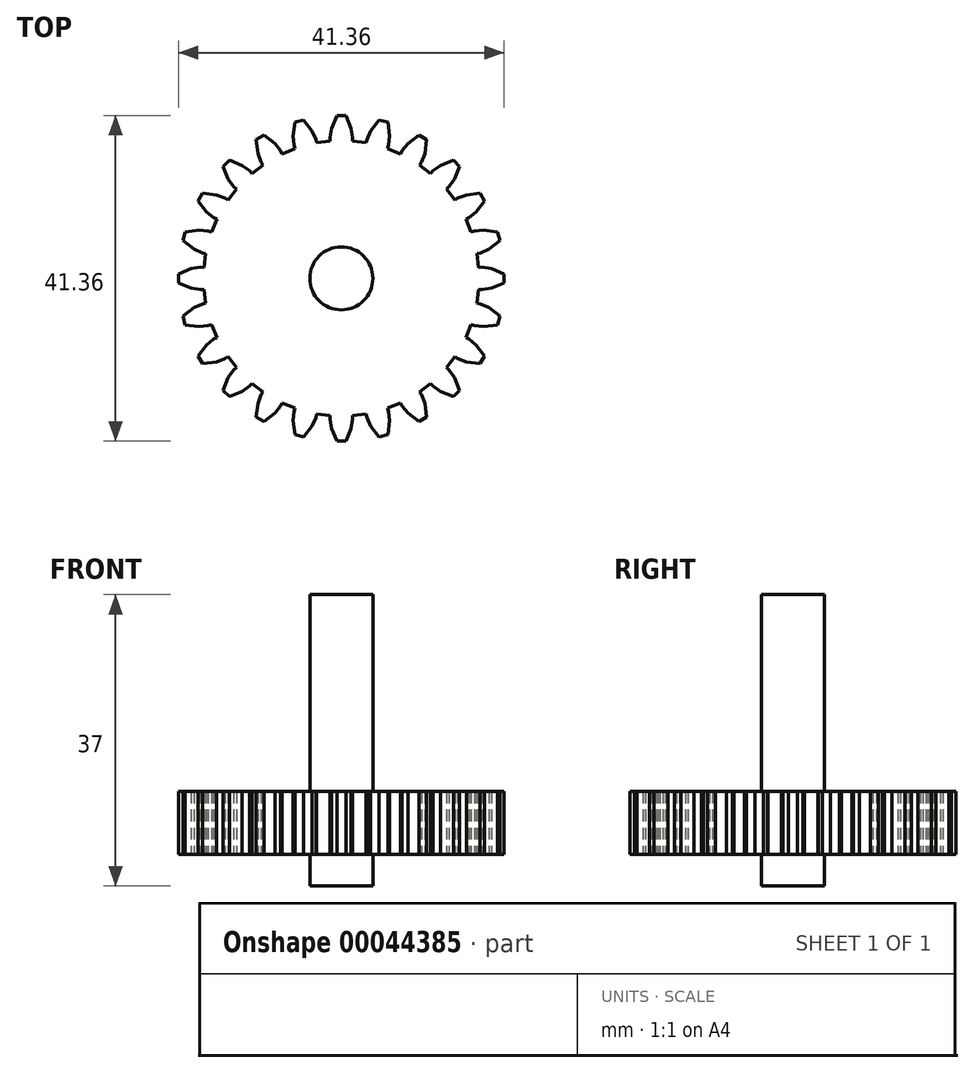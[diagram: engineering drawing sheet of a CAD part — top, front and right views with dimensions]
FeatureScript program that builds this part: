
annotation { "Feature Type Name" : "Feature", "Feature Type Description" : "" }
export const myFeature = defineFeature(function(context is Context, id is Id, definition is map)
    precondition{}
    {
        {
            var Q0;
            Q0=qCreatedBy(makeId("Top.planeOp"),FACE);
            var sketch = newSketch(context, id + "F0", { "sketchPlane" : qUnion([Q0])});
            skLineSegment(sketch, "E0", {"start": v(17.45, 1.4) * mm, "end": v(17.89, 1.44) * mm});
            skLineSegment(sketch, "E1", {"start": v(17.89, 1.44) * mm, "end": v(19.06, 1.25) * mm});
            skLineSegment(sketch, "E2", {"start": v(19.06, 1.25) * mm, "end": v(20.68, 0.57) * mm});
            skLineSegment(sketch, "E3", {"start": v(20.68, 0.57) * mm, "end": v(20.68, -0.57) * mm});
            skLineSegment(sketch, "E4", {"start": v(20.68, -0.57) * mm, "end": v(19.06, -1.25) * mm});
            skLineSegment(sketch, "E5", {"start": v(19.06, -1.25) * mm, "end": v(17.89, -1.44) * mm});
            skLineSegment(sketch, "E6", {"start": v(17.89, -1.44) * mm, "end": v(17.45, -1.4) * mm});
            skLineSegment(sketch, "E7", {"start": v(17.45, -1.4) * mm, "end": v(17.22, -3.16) * mm});
            skLineSegment(sketch, "E8", {"start": v(17.22, -3.16) * mm, "end": v(17.65, -3.24) * mm});
            skLineSegment(sketch, "E9", {"start": v(17.65, -3.24) * mm, "end": v(18.73, -3.73) * mm});
            skLineSegment(sketch, "E10", {"start": v(18.73, -3.73) * mm, "end": v(20.12, -4.8) * mm});
            skLineSegment(sketch, "E11", {"start": v(20.12, -4.8) * mm, "end": v(19.83, -5.9) * mm});
            skLineSegment(sketch, "E12", {"start": v(19.83, -5.9) * mm, "end": v(18.09, -6.14) * mm});
            skLineSegment(sketch, "E13", {"start": v(18.09, -6.14) * mm, "end": v(16.9, -6.02) * mm});
            skLineSegment(sketch, "E14", {"start": v(16.9, -6.02) * mm, "end": v(16.5, -5.87) * mm});
            skLineSegment(sketch, "E15", {"start": v(16.5, -5.87) * mm, "end": v(15.82, -7.5) * mm});
            skLineSegment(sketch, "E16", {"start": v(15.82, -7.5) * mm, "end": v(16.21, -7.7) * mm});
            skLineSegment(sketch, "E17", {"start": v(16.21, -7.7) * mm, "end": v(17.13, -8.45) * mm});
            skLineSegment(sketch, "E18", {"start": v(17.13, -8.45) * mm, "end": v(18.2, -9.85) * mm});
            skLineSegment(sketch, "E19", {"start": v(18.2, -9.85) * mm, "end": v(17.63, -10.83) * mm});
            skLineSegment(sketch, "E20", {"start": v(17.63, -10.83) * mm, "end": v(15.88, -10.61) * mm});
            skLineSegment(sketch, "E21", {"start": v(15.88, -10.61) * mm, "end": v(14.77, -10.2) * mm});
            skLineSegment(sketch, "E22", {"start": v(14.77, -10.2) * mm, "end": v(14.4, -9.94) * mm});
            skLineSegment(sketch, "E23", {"start": v(14.4, -9.94) * mm, "end": v(13.33, -11.35) * mm});
            skLineSegment(sketch, "E24", {"start": v(13.33, -11.35) * mm, "end": v(13.67, -11.63) * mm});
            skLineSegment(sketch, "E25", {"start": v(13.67, -11.63) * mm, "end": v(14.36, -12.6) * mm});
            skLineSegment(sketch, "E26", {"start": v(14.36, -12.6) * mm, "end": v(15.03, -14.22) * mm});
            skLineSegment(sketch, "E27", {"start": v(15.03, -14.22) * mm, "end": v(14.22, -15.03) * mm});
            skLineSegment(sketch, "E28", {"start": v(14.22, -15.03) * mm, "end": v(12.6, -14.36) * mm});
            skLineSegment(sketch, "E29", {"start": v(12.6, -14.36) * mm, "end": v(11.63, -13.67) * mm});
            skLineSegment(sketch, "E30", {"start": v(11.63, -13.67) * mm, "end": v(11.35, -13.33) * mm});
            skLineSegment(sketch, "E31", {"start": v(11.35, -13.33) * mm, "end": v(9.94, -14.4) * mm});
            skLineSegment(sketch, "E32", {"start": v(9.94, -14.4) * mm, "end": v(10.2, -14.77) * mm});
            skLineSegment(sketch, "E33", {"start": v(10.2, -14.77) * mm, "end": v(10.61, -15.88) * mm});
            skLineSegment(sketch, "E34", {"start": v(10.61, -15.88) * mm, "end": v(10.83, -17.63) * mm});
            skLineSegment(sketch, "E35", {"start": v(10.83, -17.63) * mm, "end": v(9.85, -18.2) * mm});
            skLineSegment(sketch, "E36", {"start": v(9.85, -18.2) * mm, "end": v(8.45, -17.13) * mm});
            skLineSegment(sketch, "E37", {"start": v(8.45, -17.13) * mm, "end": v(7.7, -16.21) * mm});
            skLineSegment(sketch, "E38", {"start": v(7.7, -16.21) * mm, "end": v(7.5, -15.82) * mm});
            skLineSegment(sketch, "E39", {"start": v(7.5, -15.82) * mm, "end": v(5.87, -16.5) * mm});
            skLineSegment(sketch, "E40", {"start": v(5.87, -16.5) * mm, "end": v(6.02, -16.9) * mm});
            skLineSegment(sketch, "E41", {"start": v(6.02, -16.9) * mm, "end": v(6.14, -18.09) * mm});
            skLineSegment(sketch, "E42", {"start": v(6.14, -18.09) * mm, "end": v(5.9, -19.83) * mm});
            skLineSegment(sketch, "E43", {"start": v(5.9, -19.83) * mm, "end": v(4.8, -20.12) * mm});
            skLineSegment(sketch, "E44", {"start": v(4.8, -20.12) * mm, "end": v(3.73, -18.73) * mm});
            skLineSegment(sketch, "E45", {"start": v(3.73, -18.73) * mm, "end": v(3.24, -17.65) * mm});
            skLineSegment(sketch, "E46", {"start": v(3.24, -17.65) * mm, "end": v(3.16, -17.22) * mm});
            skLineSegment(sketch, "E47", {"start": v(3.16, -17.22) * mm, "end": v(1.4, -17.45) * mm});
            skLineSegment(sketch, "E48", {"start": v(1.4, -17.45) * mm, "end": v(1.44, -17.89) * mm});
            skLineSegment(sketch, "E49", {"start": v(1.44, -17.89) * mm, "end": v(1.25, -19.06) * mm});
            skLineSegment(sketch, "E50", {"start": v(1.25, -19.06) * mm, "end": v(0.57, -20.68) * mm});
            skLineSegment(sketch, "E51", {"start": v(0.57, -20.68) * mm, "end": v(-0.57, -20.68) * mm});
            skLineSegment(sketch, "E52", {"start": v(-0.57, -20.68) * mm, "end": v(-1.25, -19.06) * mm});
            skLineSegment(sketch, "E53", {"start": v(-1.25, -19.06) * mm, "end": v(-1.44, -17.89) * mm});
            skLineSegment(sketch, "E54", {"start": v(-1.44, -17.89) * mm, "end": v(-1.4, -17.45) * mm});
            skLineSegment(sketch, "E55", {"start": v(-1.4, -17.45) * mm, "end": v(-3.16, -17.22) * mm});
            skLineSegment(sketch, "E56", {"start": v(-3.16, -17.22) * mm, "end": v(-3.24, -17.65) * mm});
            skLineSegment(sketch, "E57", {"start": v(-3.24, -17.65) * mm, "end": v(-3.73, -18.73) * mm});
            skLineSegment(sketch, "E58", {"start": v(-3.73, -18.73) * mm, "end": v(-4.8, -20.12) * mm});
            skLineSegment(sketch, "E59", {"start": v(-4.8, -20.12) * mm, "end": v(-5.9, -19.83) * mm});
            skLineSegment(sketch, "E60", {"start": v(-5.9, -19.83) * mm, "end": v(-6.14, -18.09) * mm});
            skLineSegment(sketch, "E61", {"start": v(-6.14, -18.09) * mm, "end": v(-6.02, -16.9) * mm});
            skLineSegment(sketch, "E62", {"start": v(-6.02, -16.9) * mm, "end": v(-5.87, -16.5) * mm});
            skLineSegment(sketch, "E63", {"start": v(-5.87, -16.5) * mm, "end": v(-7.5, -15.82) * mm});
            skLineSegment(sketch, "E64", {"start": v(-7.5, -15.82) * mm, "end": v(-7.7, -16.21) * mm});
            skLineSegment(sketch, "E65", {"start": v(-7.7, -16.21) * mm, "end": v(-8.45, -17.13) * mm});
            skLineSegment(sketch, "E66", {"start": v(-8.45, -17.13) * mm, "end": v(-9.85, -18.2) * mm});
            skLineSegment(sketch, "E67", {"start": v(-9.85, -18.2) * mm, "end": v(-10.83, -17.63) * mm});
            skLineSegment(sketch, "E68", {"start": v(-10.83, -17.63) * mm, "end": v(-10.61, -15.88) * mm});
            skLineSegment(sketch, "E69", {"start": v(-10.61, -15.88) * mm, "end": v(-10.2, -14.77) * mm});
            skLineSegment(sketch, "E70", {"start": v(-10.2, -14.77) * mm, "end": v(-9.94, -14.4) * mm});
            skLineSegment(sketch, "E71", {"start": v(-9.94, -14.4) * mm, "end": v(-11.35, -13.33) * mm});
            skLineSegment(sketch, "E72", {"start": v(-11.35, -13.33) * mm, "end": v(-11.63, -13.67) * mm});
            skLineSegment(sketch, "E73", {"start": v(-11.63, -13.67) * mm, "end": v(-12.6, -14.36) * mm});
            skLineSegment(sketch, "E74", {"start": v(-12.6, -14.36) * mm, "end": v(-14.22, -15.03) * mm});
            skLineSegment(sketch, "E75", {"start": v(-14.22, -15.03) * mm, "end": v(-15.03, -14.22) * mm});
            skLineSegment(sketch, "E76", {"start": v(-15.03, -14.22) * mm, "end": v(-14.36, -12.6) * mm});
            skLineSegment(sketch, "E77", {"start": v(-14.36, -12.6) * mm, "end": v(-13.67, -11.63) * mm});
            skLineSegment(sketch, "E78", {"start": v(-13.67, -11.63) * mm, "end": v(-13.33, -11.35) * mm});
            skLineSegment(sketch, "E79", {"start": v(-13.33, -11.35) * mm, "end": v(-14.4, -9.94) * mm});
            skLineSegment(sketch, "E80", {"start": v(-14.4, -9.94) * mm, "end": v(-14.77, -10.2) * mm});
            skLineSegment(sketch, "E81", {"start": v(-14.77, -10.2) * mm, "end": v(-15.88, -10.61) * mm});
            skLineSegment(sketch, "E82", {"start": v(-15.88, -10.61) * mm, "end": v(-17.63, -10.83) * mm});
            skLineSegment(sketch, "E83", {"start": v(-17.63, -10.83) * mm, "end": v(-18.2, -9.85) * mm});
            skLineSegment(sketch, "E84", {"start": v(-18.2, -9.85) * mm, "end": v(-17.13, -8.45) * mm});
            skLineSegment(sketch, "E85", {"start": v(-17.13, -8.45) * mm, "end": v(-16.21, -7.7) * mm});
            skLineSegment(sketch, "E86", {"start": v(-16.21, -7.7) * mm, "end": v(-15.82, -7.5) * mm});
            skLineSegment(sketch, "E87", {"start": v(-15.82, -7.5) * mm, "end": v(-16.5, -5.87) * mm});
            skLineSegment(sketch, "E88", {"start": v(-16.5, -5.87) * mm, "end": v(-16.9, -6.02) * mm});
            skLineSegment(sketch, "E89", {"start": v(-16.9, -6.02) * mm, "end": v(-18.09, -6.14) * mm});
            skLineSegment(sketch, "E90", {"start": v(-18.09, -6.14) * mm, "end": v(-19.83, -5.9) * mm});
            skLineSegment(sketch, "E91", {"start": v(-19.83, -5.9) * mm, "end": v(-20.12, -4.8) * mm});
            skLineSegment(sketch, "E92", {"start": v(-20.12, -4.8) * mm, "end": v(-18.73, -3.73) * mm});
            skLineSegment(sketch, "E93", {"start": v(-18.73, -3.73) * mm, "end": v(-17.65, -3.24) * mm});
            skLineSegment(sketch, "E94", {"start": v(-17.65, -3.24) * mm, "end": v(-17.22, -3.16) * mm});
            skLineSegment(sketch, "E95", {"start": v(-17.22, -3.16) * mm, "end": v(-17.45, -1.4) * mm});
            skLineSegment(sketch, "E96", {"start": v(-17.45, -1.4) * mm, "end": v(-17.89, -1.44) * mm});
            skLineSegment(sketch, "E97", {"start": v(-17.89, -1.44) * mm, "end": v(-19.06, -1.25) * mm});
            skLineSegment(sketch, "E98", {"start": v(-19.06, -1.25) * mm, "end": v(-20.68, -0.57) * mm});
            skLineSegment(sketch, "E99", {"start": v(-20.68, -0.57) * mm, "end": v(-20.68, 0.57) * mm});
            skLineSegment(sketch, "E100", {"start": v(-20.68, 0.57) * mm, "end": v(-19.06, 1.25) * mm});
            skLineSegment(sketch, "E101", {"start": v(-19.06, 1.25) * mm, "end": v(-17.89, 1.44) * mm});
            skLineSegment(sketch, "E102", {"start": v(-17.89, 1.44) * mm, "end": v(-17.45, 1.4) * mm});
            skLineSegment(sketch, "E103", {"start": v(-17.45, 1.4) * mm, "end": v(-17.22, 3.16) * mm});
            skLineSegment(sketch, "E104", {"start": v(-17.22, 3.16) * mm, "end": v(-17.65, 3.24) * mm});
            skLineSegment(sketch, "E105", {"start": v(-17.65, 3.24) * mm, "end": v(-18.73, 3.73) * mm});
            skLineSegment(sketch, "E106", {"start": v(-18.73, 3.73) * mm, "end": v(-20.12, 4.8) * mm});
            skLineSegment(sketch, "E107", {"start": v(-20.12, 4.8) * mm, "end": v(-19.83, 5.9) * mm});
            skLineSegment(sketch, "E108", {"start": v(-19.83, 5.9) * mm, "end": v(-18.09, 6.14) * mm});
            skLineSegment(sketch, "E109", {"start": v(-18.09, 6.14) * mm, "end": v(-16.9, 6.02) * mm});
            skLineSegment(sketch, "E110", {"start": v(-16.9, 6.02) * mm, "end": v(-16.5, 5.87) * mm});
            skLineSegment(sketch, "E111", {"start": v(-16.5, 5.87) * mm, "end": v(-15.82, 7.5) * mm});
            skLineSegment(sketch, "E112", {"start": v(-15.82, 7.5) * mm, "end": v(-16.21, 7.7) * mm});
            skLineSegment(sketch, "E113", {"start": v(-16.21, 7.7) * mm, "end": v(-17.13, 8.45) * mm});
            skLineSegment(sketch, "E114", {"start": v(-17.13, 8.45) * mm, "end": v(-18.2, 9.85) * mm});
            skLineSegment(sketch, "E115", {"start": v(-18.2, 9.85) * mm, "end": v(-17.63, 10.83) * mm});
            skLineSegment(sketch, "E116", {"start": v(-17.63, 10.83) * mm, "end": v(-15.88, 10.61) * mm});
            skLineSegment(sketch, "E117", {"start": v(-15.88, 10.61) * mm, "end": v(-14.77, 10.2) * mm});
            skLineSegment(sketch, "E118", {"start": v(-14.77, 10.2) * mm, "end": v(-14.4, 9.94) * mm});
            skLineSegment(sketch, "E119", {"start": v(-14.4, 9.94) * mm, "end": v(-13.33, 11.35) * mm});
            skLineSegment(sketch, "E120", {"start": v(-13.33, 11.35) * mm, "end": v(-13.67, 11.63) * mm});
            skLineSegment(sketch, "E121", {"start": v(-13.67, 11.63) * mm, "end": v(-14.36, 12.6) * mm});
            skLineSegment(sketch, "E122", {"start": v(-14.36, 12.6) * mm, "end": v(-15.03, 14.22) * mm});
            skLineSegment(sketch, "E123", {"start": v(-15.03, 14.22) * mm, "end": v(-14.22, 15.03) * mm});
            skLineSegment(sketch, "E124", {"start": v(-14.22, 15.03) * mm, "end": v(-12.6, 14.36) * mm});
            skLineSegment(sketch, "E125", {"start": v(-12.6, 14.36) * mm, "end": v(-11.63, 13.67) * mm});
            skLineSegment(sketch, "E126", {"start": v(-11.63, 13.67) * mm, "end": v(-11.35, 13.33) * mm});
            skLineSegment(sketch, "E127", {"start": v(-11.35, 13.33) * mm, "end": v(-9.94, 14.4) * mm});
            skLineSegment(sketch, "E128", {"start": v(-9.94, 14.4) * mm, "end": v(-10.2, 14.77) * mm});
            skLineSegment(sketch, "E129", {"start": v(-10.2, 14.77) * mm, "end": v(-10.61, 15.88) * mm});
            skLineSegment(sketch, "E130", {"start": v(-10.61, 15.88) * mm, "end": v(-10.83, 17.63) * mm});
            skLineSegment(sketch, "E131", {"start": v(-10.83, 17.63) * mm, "end": v(-9.85, 18.2) * mm});
            skLineSegment(sketch, "E132", {"start": v(-9.85, 18.2) * mm, "end": v(-8.45, 17.13) * mm});
            skLineSegment(sketch, "E133", {"start": v(-8.45, 17.13) * mm, "end": v(-7.7, 16.21) * mm});
            skLineSegment(sketch, "E134", {"start": v(-7.7, 16.21) * mm, "end": v(-7.5, 15.82) * mm});
            skLineSegment(sketch, "E135", {"start": v(-7.5, 15.82) * mm, "end": v(-5.87, 16.5) * mm});
            skLineSegment(sketch, "E136", {"start": v(-5.87, 16.5) * mm, "end": v(-6.02, 16.9) * mm});
            skLineSegment(sketch, "E137", {"start": v(-6.02, 16.9) * mm, "end": v(-6.14, 18.09) * mm});
            skLineSegment(sketch, "E138", {"start": v(-6.14, 18.09) * mm, "end": v(-5.9, 19.83) * mm});
            skLineSegment(sketch, "E139", {"start": v(-5.9, 19.83) * mm, "end": v(-4.8, 20.12) * mm});
            skLineSegment(sketch, "E140", {"start": v(-4.8, 20.12) * mm, "end": v(-3.73, 18.73) * mm});
            skLineSegment(sketch, "E141", {"start": v(-3.73, 18.73) * mm, "end": v(-3.24, 17.65) * mm});
            skLineSegment(sketch, "E142", {"start": v(-3.24, 17.65) * mm, "end": v(-3.16, 17.22) * mm});
            skLineSegment(sketch, "E143", {"start": v(-3.16, 17.22) * mm, "end": v(-1.4, 17.45) * mm});
            skLineSegment(sketch, "E144", {"start": v(-1.4, 17.45) * mm, "end": v(-1.44, 17.89) * mm});
            skLineSegment(sketch, "E145", {"start": v(-1.44, 17.89) * mm, "end": v(-1.25, 19.06) * mm});
            skLineSegment(sketch, "E146", {"start": v(-1.25, 19.06) * mm, "end": v(-0.57, 20.68) * mm});
            skLineSegment(sketch, "E147", {"start": v(-0.57, 20.68) * mm, "end": v(0.57, 20.68) * mm});
            skLineSegment(sketch, "E148", {"start": v(0.57, 20.68) * mm, "end": v(1.25, 19.06) * mm});
            skLineSegment(sketch, "E149", {"start": v(1.25, 19.06) * mm, "end": v(1.44, 17.89) * mm});
            skLineSegment(sketch, "E150", {"start": v(1.44, 17.89) * mm, "end": v(1.4, 17.45) * mm});
            skLineSegment(sketch, "E151", {"start": v(1.4, 17.45) * mm, "end": v(3.16, 17.22) * mm});
            skLineSegment(sketch, "E152", {"start": v(3.16, 17.22) * mm, "end": v(3.24, 17.65) * mm});
            skLineSegment(sketch, "E153", {"start": v(3.24, 17.65) * mm, "end": v(3.73, 18.73) * mm});
            skLineSegment(sketch, "E154", {"start": v(3.73, 18.73) * mm, "end": v(4.8, 20.12) * mm});
            skLineSegment(sketch, "E155", {"start": v(4.8, 20.12) * mm, "end": v(5.9, 19.83) * mm});
            skLineSegment(sketch, "E156", {"start": v(5.9, 19.83) * mm, "end": v(6.14, 18.09) * mm});
            skLineSegment(sketch, "E157", {"start": v(6.14, 18.09) * mm, "end": v(6.02, 16.9) * mm});
            skLineSegment(sketch, "E158", {"start": v(6.02, 16.9) * mm, "end": v(5.87, 16.5) * mm});
            skLineSegment(sketch, "E159", {"start": v(5.87, 16.5) * mm, "end": v(7.5, 15.82) * mm});
            skLineSegment(sketch, "E160", {"start": v(7.5, 15.82) * mm, "end": v(7.7, 16.21) * mm});
            skLineSegment(sketch, "E161", {"start": v(7.7, 16.21) * mm, "end": v(8.45, 17.13) * mm});
            skLineSegment(sketch, "E162", {"start": v(8.45, 17.13) * mm, "end": v(9.85, 18.2) * mm});
            skLineSegment(sketch, "E163", {"start": v(9.85, 18.2) * mm, "end": v(10.83, 17.63) * mm});
            skLineSegment(sketch, "E164", {"start": v(10.83, 17.63) * mm, "end": v(10.61, 15.88) * mm});
            skLineSegment(sketch, "E165", {"start": v(10.61, 15.88) * mm, "end": v(10.2, 14.77) * mm});
            skLineSegment(sketch, "E166", {"start": v(10.2, 14.77) * mm, "end": v(9.94, 14.4) * mm});
            skLineSegment(sketch, "E167", {"start": v(9.94, 14.4) * mm, "end": v(11.35, 13.33) * mm});
            skLineSegment(sketch, "E168", {"start": v(11.35, 13.33) * mm, "end": v(11.63, 13.67) * mm});
            skLineSegment(sketch, "E169", {"start": v(11.63, 13.67) * mm, "end": v(12.6, 14.36) * mm});
            skLineSegment(sketch, "E170", {"start": v(12.6, 14.36) * mm, "end": v(14.22, 15.03) * mm});
            skLineSegment(sketch, "E171", {"start": v(14.22, 15.03) * mm, "end": v(15.03, 14.22) * mm});
            skLineSegment(sketch, "E172", {"start": v(15.03, 14.22) * mm, "end": v(14.36, 12.6) * mm});
            skLineSegment(sketch, "E173", {"start": v(14.36, 12.6) * mm, "end": v(13.67, 11.63) * mm});
            skLineSegment(sketch, "E174", {"start": v(13.67, 11.63) * mm, "end": v(13.33, 11.35) * mm});
            skLineSegment(sketch, "E175", {"start": v(13.33, 11.35) * mm, "end": v(14.4, 9.94) * mm});
            skLineSegment(sketch, "E176", {"start": v(14.4, 9.94) * mm, "end": v(14.77, 10.2) * mm});
            skLineSegment(sketch, "E177", {"start": v(14.77, 10.2) * mm, "end": v(15.88, 10.61) * mm});
            skLineSegment(sketch, "E178", {"start": v(15.88, 10.61) * mm, "end": v(17.63, 10.83) * mm});
            skLineSegment(sketch, "E179", {"start": v(17.63, 10.83) * mm, "end": v(18.2, 9.85) * mm});
            skLineSegment(sketch, "E180", {"start": v(18.2, 9.85) * mm, "end": v(17.13, 8.45) * mm});
            skLineSegment(sketch, "E181", {"start": v(17.13, 8.45) * mm, "end": v(16.21, 7.7) * mm});
            skLineSegment(sketch, "E182", {"start": v(16.21, 7.7) * mm, "end": v(15.82, 7.5) * mm});
            skLineSegment(sketch, "E183", {"start": v(15.82, 7.5) * mm, "end": v(16.5, 5.87) * mm});
            skLineSegment(sketch, "E184", {"start": v(16.5, 5.87) * mm, "end": v(16.9, 6.02) * mm});
            skLineSegment(sketch, "E185", {"start": v(16.9, 6.02) * mm, "end": v(18.09, 6.14) * mm});
            skLineSegment(sketch, "E186", {"start": v(18.09, 6.14) * mm, "end": v(19.83, 5.9) * mm});
            skLineSegment(sketch, "E187", {"start": v(19.83, 5.9) * mm, "end": v(20.12, 4.8) * mm});
            skLineSegment(sketch, "E188", {"start": v(20.12, 4.8) * mm, "end": v(18.73, 3.73) * mm});
            skLineSegment(sketch, "E189", {"start": v(18.73, 3.73) * mm, "end": v(17.65, 3.24) * mm});
            skLineSegment(sketch, "E190", {"start": v(17.65, 3.24) * mm, "end": v(17.22, 3.16) * mm});
            skLineSegment(sketch, "E191", {"start": v(17.22, 3.16) * mm, "end": v(17.45, 1.4) * mm});
            skSolve(sketch);
        }
        {
            var Q0;
            Q0=makeQuery(id+"F0.imprint","IMPRINT",FACE,{"disambiguationData":[TD([[makeQuery(id+"F0.imprint","IMPRINT",EDGE,{"derivedFrom":sQuery(id+"F0.wireOp",EDGE,"E0")}),-1.0]])]});
            extrude(context, id + "F1", {"entities" : qUnion([Q0]), "depth" : 8 * mm});
        }
        {
            var Q0;
            Q0=makeQuery(id+"F1.opExtrude","CAP_FACE",FACE,{"disambiguationData":[OSD([sQuery(id+"F0.wireOp",EDGE,"E0"),sQuery(id+"F0.wireOp",EDGE,"E1"),sQuery(id+"F0.wireOp",EDGE,"E2"),sQuery(id+"F0.wireOp",EDGE,"E3"),sQuery(id+"F0.wireOp",EDGE,"E4"),sQuery(id+"F0.wireOp",EDGE,"E5"),sQuery(id+"F0.wireOp",EDGE,"E6"),sQuery(id+"F0.wireOp",EDGE,"E7"),sQuery(id+"F0.wireOp",EDGE,"E8"),sQuery(id+"F0.wireOp",EDGE,"E9"),sQuery(id+"F0.wireOp",EDGE,"E10"),sQuery(id+"F0.wireOp",EDGE,"E11"),sQuery(id+"F0.wireOp",EDGE,"E12"),sQuery(id+"F0.wireOp",EDGE,"E13"),sQuery(id+"F0.wireOp",EDGE,"E14"),sQuery(id+"F0.wireOp",EDGE,"E15"),sQuery(id+"F0.wireOp",EDGE,"E16"),sQuery(id+"F0.wireOp",EDGE,"E17"),sQuery(id+"F0.wireOp",EDGE,"E18"),sQuery(id+"F0.wireOp",EDGE,"E19"),sQuery(id+"F0.wireOp",EDGE,"E20"),sQuery(id+"F0.wireOp",EDGE,"E21"),sQuery(id+"F0.wireOp",EDGE,"E22"),sQuery(id+"F0.wireOp",EDGE,"E23"),sQuery(id+"F0.wireOp",EDGE,"E24"),sQuery(id+"F0.wireOp",EDGE,"E25"),sQuery(id+"F0.wireOp",EDGE,"E26"),sQuery(id+"F0.wireOp",EDGE,"E27"),sQuery(id+"F0.wireOp",EDGE,"E28"),sQuery(id+"F0.wireOp",EDGE,"E29"),sQuery(id+"F0.wireOp",EDGE,"E30"),sQuery(id+"F0.wireOp",EDGE,"E31"),sQuery(id+"F0.wireOp",EDGE,"E32"),sQuery(id+"F0.wireOp",EDGE,"E33"),sQuery(id+"F0.wireOp",EDGE,"E34"),sQuery(id+"F0.wireOp",EDGE,"E35"),sQuery(id+"F0.wireOp",EDGE,"E36"),sQuery(id+"F0.wireOp",EDGE,"E37"),sQuery(id+"F0.wireOp",EDGE,"E38"),sQuery(id+"F0.wireOp",EDGE,"E39"),sQuery(id+"F0.wireOp",EDGE,"E40"),sQuery(id+"F0.wireOp",EDGE,"E41"),sQuery(id+"F0.wireOp",EDGE,"E42"),sQuery(id+"F0.wireOp",EDGE,"E43"),sQuery(id+"F0.wireOp",EDGE,"E44"),sQuery(id+"F0.wireOp",EDGE,"E45"),sQuery(id+"F0.wireOp",EDGE,"E46"),sQuery(id+"F0.wireOp",EDGE,"E47"),sQuery(id+"F0.wireOp",EDGE,"E48"),sQuery(id+"F0.wireOp",EDGE,"E49"),sQuery(id+"F0.wireOp",EDGE,"E50"),sQuery(id+"F0.wireOp",EDGE,"E51"),sQuery(id+"F0.wireOp",EDGE,"E52"),sQuery(id+"F0.wireOp",EDGE,"E53"),sQuery(id+"F0.wireOp",EDGE,"E54"),sQuery(id+"F0.wireOp",EDGE,"E55"),sQuery(id+"F0.wireOp",EDGE,"E56"),sQuery(id+"F0.wireOp",EDGE,"E57"),sQuery(id+"F0.wireOp",EDGE,"E58"),sQuery(id+"F0.wireOp",EDGE,"E59"),sQuery(id+"F0.wireOp",EDGE,"E60"),sQuery(id+"F0.wireOp",EDGE,"E61"),sQuery(id+"F0.wireOp",EDGE,"E62"),sQuery(id+"F0.wireOp",EDGE,"E63"),sQuery(id+"F0.wireOp",EDGE,"E64"),sQuery(id+"F0.wireOp",EDGE,"E65"),sQuery(id+"F0.wireOp",EDGE,"E66"),sQuery(id+"F0.wireOp",EDGE,"E67"),sQuery(id+"F0.wireOp",EDGE,"E68"),sQuery(id+"F0.wireOp",EDGE,"E69"),sQuery(id+"F0.wireOp",EDGE,"E70"),sQuery(id+"F0.wireOp",EDGE,"E71"),sQuery(id+"F0.wireOp",EDGE,"E72"),sQuery(id+"F0.wireOp",EDGE,"E73"),sQuery(id+"F0.wireOp",EDGE,"E74"),sQuery(id+"F0.wireOp",EDGE,"E75"),sQuery(id+"F0.wireOp",EDGE,"E76"),sQuery(id+"F0.wireOp",EDGE,"E77"),sQuery(id+"F0.wireOp",EDGE,"E78"),sQuery(id+"F0.wireOp",EDGE,"E79"),sQuery(id+"F0.wireOp",EDGE,"E80"),sQuery(id+"F0.wireOp",EDGE,"E81"),sQuery(id+"F0.wireOp",EDGE,"E82"),sQuery(id+"F0.wireOp",EDGE,"E83"),sQuery(id+"F0.wireOp",EDGE,"E84"),sQuery(id+"F0.wireOp",EDGE,"E85"),sQuery(id+"F0.wireOp",EDGE,"E86"),sQuery(id+"F0.wireOp",EDGE,"E87"),sQuery(id+"F0.wireOp",EDGE,"E88"),sQuery(id+"F0.wireOp",EDGE,"E89"),sQuery(id+"F0.wireOp",EDGE,"E90"),sQuery(id+"F0.wireOp",EDGE,"E91"),sQuery(id+"F0.wireOp",EDGE,"E92"),sQuery(id+"F0.wireOp",EDGE,"E93"),sQuery(id+"F0.wireOp",EDGE,"E94"),sQuery(id+"F0.wireOp",EDGE,"E95"),sQuery(id+"F0.wireOp",EDGE,"E96"),sQuery(id+"F0.wireOp",EDGE,"E97"),sQuery(id+"F0.wireOp",EDGE,"E98"),sQuery(id+"F0.wireOp",EDGE,"E99"),sQuery(id+"F0.wireOp",EDGE,"E100"),sQuery(id+"F0.wireOp",EDGE,"E101"),sQuery(id+"F0.wireOp",EDGE,"E102"),sQuery(id+"F0.wireOp",EDGE,"E103"),sQuery(id+"F0.wireOp",EDGE,"E104"),sQuery(id+"F0.wireOp",EDGE,"E105"),sQuery(id+"F0.wireOp",EDGE,"E106"),sQuery(id+"F0.wireOp",EDGE,"E107"),sQuery(id+"F0.wireOp",EDGE,"E108"),sQuery(id+"F0.wireOp",EDGE,"E109"),sQuery(id+"F0.wireOp",EDGE,"E110"),sQuery(id+"F0.wireOp",EDGE,"E111"),sQuery(id+"F0.wireOp",EDGE,"E112"),sQuery(id+"F0.wireOp",EDGE,"E113"),sQuery(id+"F0.wireOp",EDGE,"E114"),sQuery(id+"F0.wireOp",EDGE,"E115"),sQuery(id+"F0.wireOp",EDGE,"E116"),sQuery(id+"F0.wireOp",EDGE,"E117"),sQuery(id+"F0.wireOp",EDGE,"E118"),sQuery(id+"F0.wireOp",EDGE,"E119"),sQuery(id+"F0.wireOp",EDGE,"E120"),sQuery(id+"F0.wireOp",EDGE,"E121"),sQuery(id+"F0.wireOp",EDGE,"E122"),sQuery(id+"F0.wireOp",EDGE,"E123"),sQuery(id+"F0.wireOp",EDGE,"E124"),sQuery(id+"F0.wireOp",EDGE,"E125"),sQuery(id+"F0.wireOp",EDGE,"E126"),sQuery(id+"F0.wireOp",EDGE,"E127"),sQuery(id+"F0.wireOp",EDGE,"E128"),sQuery(id+"F0.wireOp",EDGE,"E129"),sQuery(id+"F0.wireOp",EDGE,"E130"),sQuery(id+"F0.wireOp",EDGE,"E131"),sQuery(id+"F0.wireOp",EDGE,"E132"),sQuery(id+"F0.wireOp",EDGE,"E133"),sQuery(id+"F0.wireOp",EDGE,"E134"),sQuery(id+"F0.wireOp",EDGE,"E135"),sQuery(id+"F0.wireOp",EDGE,"E136"),sQuery(id+"F0.wireOp",EDGE,"E137"),sQuery(id+"F0.wireOp",EDGE,"E138"),sQuery(id+"F0.wireOp",EDGE,"E139"),sQuery(id+"F0.wireOp",EDGE,"E140"),sQuery(id+"F0.wireOp",EDGE,"E141"),sQuery(id+"F0.wireOp",EDGE,"E142"),sQuery(id+"F0.wireOp",EDGE,"E143"),sQuery(id+"F0.wireOp",EDGE,"E144"),sQuery(id+"F0.wireOp",EDGE,"E145"),sQuery(id+"F0.wireOp",EDGE,"E146"),sQuery(id+"F0.wireOp",EDGE,"E147"),sQuery(id+"F0.wireOp",EDGE,"E148"),sQuery(id+"F0.wireOp",EDGE,"E149"),sQuery(id+"F0.wireOp",EDGE,"E150"),sQuery(id+"F0.wireOp",EDGE,"E151"),sQuery(id+"F0.wireOp",EDGE,"E152"),sQuery(id+"F0.wireOp",EDGE,"E153"),sQuery(id+"F0.wireOp",EDGE,"E154"),sQuery(id+"F0.wireOp",EDGE,"E155"),sQuery(id+"F0.wireOp",EDGE,"E156"),sQuery(id+"F0.wireOp",EDGE,"E157"),sQuery(id+"F0.wireOp",EDGE,"E158"),sQuery(id+"F0.wireOp",EDGE,"E159"),sQuery(id+"F0.wireOp",EDGE,"E160"),sQuery(id+"F0.wireOp",EDGE,"E161"),sQuery(id+"F0.wireOp",EDGE,"E162"),sQuery(id+"F0.wireOp",EDGE,"E163"),sQuery(id+"F0.wireOp",EDGE,"E164"),sQuery(id+"F0.wireOp",EDGE,"E165"),sQuery(id+"F0.wireOp",EDGE,"E166"),sQuery(id+"F0.wireOp",EDGE,"E167"),sQuery(id+"F0.wireOp",EDGE,"E168"),sQuery(id+"F0.wireOp",EDGE,"E169"),sQuery(id+"F0.wireOp",EDGE,"E170"),sQuery(id+"F0.wireOp",EDGE,"E171"),sQuery(id+"F0.wireOp",EDGE,"E172"),sQuery(id+"F0.wireOp",EDGE,"E173"),sQuery(id+"F0.wireOp",EDGE,"E174"),sQuery(id+"F0.wireOp",EDGE,"E175"),sQuery(id+"F0.wireOp",EDGE,"E176"),sQuery(id+"F0.wireOp",EDGE,"E177"),sQuery(id+"F0.wireOp",EDGE,"E178"),sQuery(id+"F0.wireOp",EDGE,"E179"),sQuery(id+"F0.wireOp",EDGE,"E180"),sQuery(id+"F0.wireOp",EDGE,"E181"),sQuery(id+"F0.wireOp",EDGE,"E182"),sQuery(id+"F0.wireOp",EDGE,"E183"),sQuery(id+"F0.wireOp",EDGE,"E184"),sQuery(id+"F0.wireOp",EDGE,"E185"),sQuery(id+"F0.wireOp",EDGE,"E186"),sQuery(id+"F0.wireOp",EDGE,"E187"),sQuery(id+"F0.wireOp",EDGE,"E188"),sQuery(id+"F0.wireOp",EDGE,"E189"),sQuery(id+"F0.wireOp",EDGE,"E190"),sQuery(id+"F0.wireOp",EDGE,"E191")])],"isStart":false});
            var sketch = newSketch(context, id + "F2", { "sketchPlane" : qUnion([Q0])});
            skCircle(sketch, "E192", {"center": v(0, 0) * mm, "radius": 4 * mm});
            skSolve(sketch);
        }
        {
            var Q0;
            Q0=makeQuery(id+"F2.imprint","IMPRINT",FACE,{"disambiguationData":[TD([[makeQuery(id+"F2.imprint","IMPRINT",EDGE,{"derivedFrom":sQuery(id+"F2.wireOp",EDGE,"E192")}),1.0]])]});
            extrude(context, id + "F3", {"entities" : qUnion([Q0]), "operationType" : NewBodyOperationType.ADD, "depth" : 25 * mm});
        }
        {
            var Q0;
            Q0=makeQuery(id+"F1.opExtrude","CAP_FACE",FACE,{"disambiguationData":[OSD([sQuery(id+"F0.wireOp",EDGE,"E0"),sQuery(id+"F0.wireOp",EDGE,"E1"),sQuery(id+"F0.wireOp",EDGE,"E2"),sQuery(id+"F0.wireOp",EDGE,"E3"),sQuery(id+"F0.wireOp",EDGE,"E4"),sQuery(id+"F0.wireOp",EDGE,"E5"),sQuery(id+"F0.wireOp",EDGE,"E6"),sQuery(id+"F0.wireOp",EDGE,"E7"),sQuery(id+"F0.wireOp",EDGE,"E8"),sQuery(id+"F0.wireOp",EDGE,"E9"),sQuery(id+"F0.wireOp",EDGE,"E10"),sQuery(id+"F0.wireOp",EDGE,"E11"),sQuery(id+"F0.wireOp",EDGE,"E12"),sQuery(id+"F0.wireOp",EDGE,"E13"),sQuery(id+"F0.wireOp",EDGE,"E14"),sQuery(id+"F0.wireOp",EDGE,"E15"),sQuery(id+"F0.wireOp",EDGE,"E16"),sQuery(id+"F0.wireOp",EDGE,"E17"),sQuery(id+"F0.wireOp",EDGE,"E18"),sQuery(id+"F0.wireOp",EDGE,"E19"),sQuery(id+"F0.wireOp",EDGE,"E20"),sQuery(id+"F0.wireOp",EDGE,"E21"),sQuery(id+"F0.wireOp",EDGE,"E22"),sQuery(id+"F0.wireOp",EDGE,"E23"),sQuery(id+"F0.wireOp",EDGE,"E24"),sQuery(id+"F0.wireOp",EDGE,"E25"),sQuery(id+"F0.wireOp",EDGE,"E26"),sQuery(id+"F0.wireOp",EDGE,"E27"),sQuery(id+"F0.wireOp",EDGE,"E28"),sQuery(id+"F0.wireOp",EDGE,"E29"),sQuery(id+"F0.wireOp",EDGE,"E30"),sQuery(id+"F0.wireOp",EDGE,"E31"),sQuery(id+"F0.wireOp",EDGE,"E32"),sQuery(id+"F0.wireOp",EDGE,"E33"),sQuery(id+"F0.wireOp",EDGE,"E34"),sQuery(id+"F0.wireOp",EDGE,"E35"),sQuery(id+"F0.wireOp",EDGE,"E36"),sQuery(id+"F0.wireOp",EDGE,"E37"),sQuery(id+"F0.wireOp",EDGE,"E38"),sQuery(id+"F0.wireOp",EDGE,"E39"),sQuery(id+"F0.wireOp",EDGE,"E40"),sQuery(id+"F0.wireOp",EDGE,"E41"),sQuery(id+"F0.wireOp",EDGE,"E42"),sQuery(id+"F0.wireOp",EDGE,"E43"),sQuery(id+"F0.wireOp",EDGE,"E44"),sQuery(id+"F0.wireOp",EDGE,"E45"),sQuery(id+"F0.wireOp",EDGE,"E46"),sQuery(id+"F0.wireOp",EDGE,"E47"),sQuery(id+"F0.wireOp",EDGE,"E48"),sQuery(id+"F0.wireOp",EDGE,"E49"),sQuery(id+"F0.wireOp",EDGE,"E50"),sQuery(id+"F0.wireOp",EDGE,"E51"),sQuery(id+"F0.wireOp",EDGE,"E52"),sQuery(id+"F0.wireOp",EDGE,"E53"),sQuery(id+"F0.wireOp",EDGE,"E54"),sQuery(id+"F0.wireOp",EDGE,"E55"),sQuery(id+"F0.wireOp",EDGE,"E56"),sQuery(id+"F0.wireOp",EDGE,"E57"),sQuery(id+"F0.wireOp",EDGE,"E58"),sQuery(id+"F0.wireOp",EDGE,"E59"),sQuery(id+"F0.wireOp",EDGE,"E60"),sQuery(id+"F0.wireOp",EDGE,"E61"),sQuery(id+"F0.wireOp",EDGE,"E62"),sQuery(id+"F0.wireOp",EDGE,"E63"),sQuery(id+"F0.wireOp",EDGE,"E64"),sQuery(id+"F0.wireOp",EDGE,"E65"),sQuery(id+"F0.wireOp",EDGE,"E66"),sQuery(id+"F0.wireOp",EDGE,"E67"),sQuery(id+"F0.wireOp",EDGE,"E68"),sQuery(id+"F0.wireOp",EDGE,"E69"),sQuery(id+"F0.wireOp",EDGE,"E70"),sQuery(id+"F0.wireOp",EDGE,"E71"),sQuery(id+"F0.wireOp",EDGE,"E72"),sQuery(id+"F0.wireOp",EDGE,"E73"),sQuery(id+"F0.wireOp",EDGE,"E74"),sQuery(id+"F0.wireOp",EDGE,"E75"),sQuery(id+"F0.wireOp",EDGE,"E76"),sQuery(id+"F0.wireOp",EDGE,"E77"),sQuery(id+"F0.wireOp",EDGE,"E78"),sQuery(id+"F0.wireOp",EDGE,"E79"),sQuery(id+"F0.wireOp",EDGE,"E80"),sQuery(id+"F0.wireOp",EDGE,"E81"),sQuery(id+"F0.wireOp",EDGE,"E82"),sQuery(id+"F0.wireOp",EDGE,"E83"),sQuery(id+"F0.wireOp",EDGE,"E84"),sQuery(id+"F0.wireOp",EDGE,"E85"),sQuery(id+"F0.wireOp",EDGE,"E86"),sQuery(id+"F0.wireOp",EDGE,"E87"),sQuery(id+"F0.wireOp",EDGE,"E88"),sQuery(id+"F0.wireOp",EDGE,"E89"),sQuery(id+"F0.wireOp",EDGE,"E90"),sQuery(id+"F0.wireOp",EDGE,"E91"),sQuery(id+"F0.wireOp",EDGE,"E92"),sQuery(id+"F0.wireOp",EDGE,"E93"),sQuery(id+"F0.wireOp",EDGE,"E94"),sQuery(id+"F0.wireOp",EDGE,"E95"),sQuery(id+"F0.wireOp",EDGE,"E96"),sQuery(id+"F0.wireOp",EDGE,"E97"),sQuery(id+"F0.wireOp",EDGE,"E98"),sQuery(id+"F0.wireOp",EDGE,"E99"),sQuery(id+"F0.wireOp",EDGE,"E100"),sQuery(id+"F0.wireOp",EDGE,"E101"),sQuery(id+"F0.wireOp",EDGE,"E102"),sQuery(id+"F0.wireOp",EDGE,"E103"),sQuery(id+"F0.wireOp",EDGE,"E104"),sQuery(id+"F0.wireOp",EDGE,"E105"),sQuery(id+"F0.wireOp",EDGE,"E106"),sQuery(id+"F0.wireOp",EDGE,"E107"),sQuery(id+"F0.wireOp",EDGE,"E108"),sQuery(id+"F0.wireOp",EDGE,"E109"),sQuery(id+"F0.wireOp",EDGE,"E110"),sQuery(id+"F0.wireOp",EDGE,"E111"),sQuery(id+"F0.wireOp",EDGE,"E112"),sQuery(id+"F0.wireOp",EDGE,"E113"),sQuery(id+"F0.wireOp",EDGE,"E114"),sQuery(id+"F0.wireOp",EDGE,"E115"),sQuery(id+"F0.wireOp",EDGE,"E116"),sQuery(id+"F0.wireOp",EDGE,"E117"),sQuery(id+"F0.wireOp",EDGE,"E118"),sQuery(id+"F0.wireOp",EDGE,"E119"),sQuery(id+"F0.wireOp",EDGE,"E120"),sQuery(id+"F0.wireOp",EDGE,"E121"),sQuery(id+"F0.wireOp",EDGE,"E122"),sQuery(id+"F0.wireOp",EDGE,"E123"),sQuery(id+"F0.wireOp",EDGE,"E124"),sQuery(id+"F0.wireOp",EDGE,"E125"),sQuery(id+"F0.wireOp",EDGE,"E126"),sQuery(id+"F0.wireOp",EDGE,"E127"),sQuery(id+"F0.wireOp",EDGE,"E128"),sQuery(id+"F0.wireOp",EDGE,"E129"),sQuery(id+"F0.wireOp",EDGE,"E130"),sQuery(id+"F0.wireOp",EDGE,"E131"),sQuery(id+"F0.wireOp",EDGE,"E132"),sQuery(id+"F0.wireOp",EDGE,"E133"),sQuery(id+"F0.wireOp",EDGE,"E134"),sQuery(id+"F0.wireOp",EDGE,"E135"),sQuery(id+"F0.wireOp",EDGE,"E136"),sQuery(id+"F0.wireOp",EDGE,"E137"),sQuery(id+"F0.wireOp",EDGE,"E138"),sQuery(id+"F0.wireOp",EDGE,"E139"),sQuery(id+"F0.wireOp",EDGE,"E140"),sQuery(id+"F0.wireOp",EDGE,"E141"),sQuery(id+"F0.wireOp",EDGE,"E142"),sQuery(id+"F0.wireOp",EDGE,"E143"),sQuery(id+"F0.wireOp",EDGE,"E144"),sQuery(id+"F0.wireOp",EDGE,"E145"),sQuery(id+"F0.wireOp",EDGE,"E146"),sQuery(id+"F0.wireOp",EDGE,"E147"),sQuery(id+"F0.wireOp",EDGE,"E148"),sQuery(id+"F0.wireOp",EDGE,"E149"),sQuery(id+"F0.wireOp",EDGE,"E150"),sQuery(id+"F0.wireOp",EDGE,"E151"),sQuery(id+"F0.wireOp",EDGE,"E152"),sQuery(id+"F0.wireOp",EDGE,"E153"),sQuery(id+"F0.wireOp",EDGE,"E154"),sQuery(id+"F0.wireOp",EDGE,"E155"),sQuery(id+"F0.wireOp",EDGE,"E156"),sQuery(id+"F0.wireOp",EDGE,"E157"),sQuery(id+"F0.wireOp",EDGE,"E158"),sQuery(id+"F0.wireOp",EDGE,"E159"),sQuery(id+"F0.wireOp",EDGE,"E160"),sQuery(id+"F0.wireOp",EDGE,"E161"),sQuery(id+"F0.wireOp",EDGE,"E162"),sQuery(id+"F0.wireOp",EDGE,"E163"),sQuery(id+"F0.wireOp",EDGE,"E164"),sQuery(id+"F0.wireOp",EDGE,"E165"),sQuery(id+"F0.wireOp",EDGE,"E166"),sQuery(id+"F0.wireOp",EDGE,"E167"),sQuery(id+"F0.wireOp",EDGE,"E168"),sQuery(id+"F0.wireOp",EDGE,"E169"),sQuery(id+"F0.wireOp",EDGE,"E170"),sQuery(id+"F0.wireOp",EDGE,"E171"),sQuery(id+"F0.wireOp",EDGE,"E172"),sQuery(id+"F0.wireOp",EDGE,"E173"),sQuery(id+"F0.wireOp",EDGE,"E174"),sQuery(id+"F0.wireOp",EDGE,"E175"),sQuery(id+"F0.wireOp",EDGE,"E176"),sQuery(id+"F0.wireOp",EDGE,"E177"),sQuery(id+"F0.wireOp",EDGE,"E178"),sQuery(id+"F0.wireOp",EDGE,"E179"),sQuery(id+"F0.wireOp",EDGE,"E180"),sQuery(id+"F0.wireOp",EDGE,"E181"),sQuery(id+"F0.wireOp",EDGE,"E182"),sQuery(id+"F0.wireOp",EDGE,"E183"),sQuery(id+"F0.wireOp",EDGE,"E184"),sQuery(id+"F0.wireOp",EDGE,"E185"),sQuery(id+"F0.wireOp",EDGE,"E186"),sQuery(id+"F0.wireOp",EDGE,"E187"),sQuery(id+"F0.wireOp",EDGE,"E188"),sQuery(id+"F0.wireOp",EDGE,"E189"),sQuery(id+"F0.wireOp",EDGE,"E190"),sQuery(id+"F0.wireOp",EDGE,"E191")])],"isStart":true});
            var sketch = newSketch(context, id + "F4", { "sketchPlane" : qUnion([Q0])});
            skCircle(sketch, "E193", {"center": v(0, 0) * mm, "radius": 4 * mm});
            skSolve(sketch);
        }
        {
            var Q0;
            Q0=makeQuery(id+"F4.imprint","IMPRINT",FACE,{"disambiguationData":[TD([[makeQuery(id+"F4.imprint","IMPRINT",EDGE,{"derivedFrom":sQuery(id+"F4.wireOp",EDGE,"E193")}),1.0]])]});
            extrude(context, id + "F5", {"entities" : qUnion([Q0]), "operationType" : NewBodyOperationType.ADD, "depth" : 4 * mm});
        }
    });
